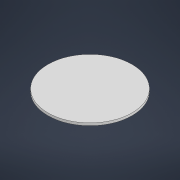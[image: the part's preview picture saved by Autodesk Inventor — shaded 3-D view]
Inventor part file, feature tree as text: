
AUTODESK INVENTOR PART (.ipt)
format: ipt  version: 2022 (Build 260153070, 153G)  size: 86,016 bytes
history: native  units: mm
features: other x1, extrude x1, sketch x1
ambient origin geometry x8: Origin, YZ Plane, XZ Plane, XY Plane, X Axis, Y Axis, Z Axis, Center Point
bodies: Body1 (feature_tree)
feature tree (3):
  other  "Твердое тело1"
  extrude  "Выдавливание1"  Depth=105.0mm
  sketch  "Эскиз1"
